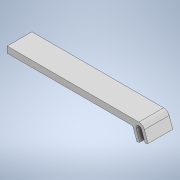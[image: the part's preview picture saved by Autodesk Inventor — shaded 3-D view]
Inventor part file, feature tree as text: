
AUTODESK INVENTOR PART (.ipt)
format: ipt  version: 2021 (Build 250183000, 183)  size: 141,824 bytes
history: native  units: mm
features: extrude x1, sketch x1
ambient origin geometry x8: Origin, YZ Plane, XZ Plane, XY Plane, X Axis, Y Axis, Z Axis, Center Point
bodies: Solid1 (feature_tree)
feature tree (2):
  extrude  "Extrusion1"  Depth=10.0mm
  sketch  "Sketch1"  dims[d31=80.0mm d32=0.0mm d38=10.0mm d39=10.0mm d40=9.0mm d47=20.0mm d53=9.0mm d56=400.0mm d58=200.0mm d59=35.0mm d60=3.490659mm d61=100.0mm]
